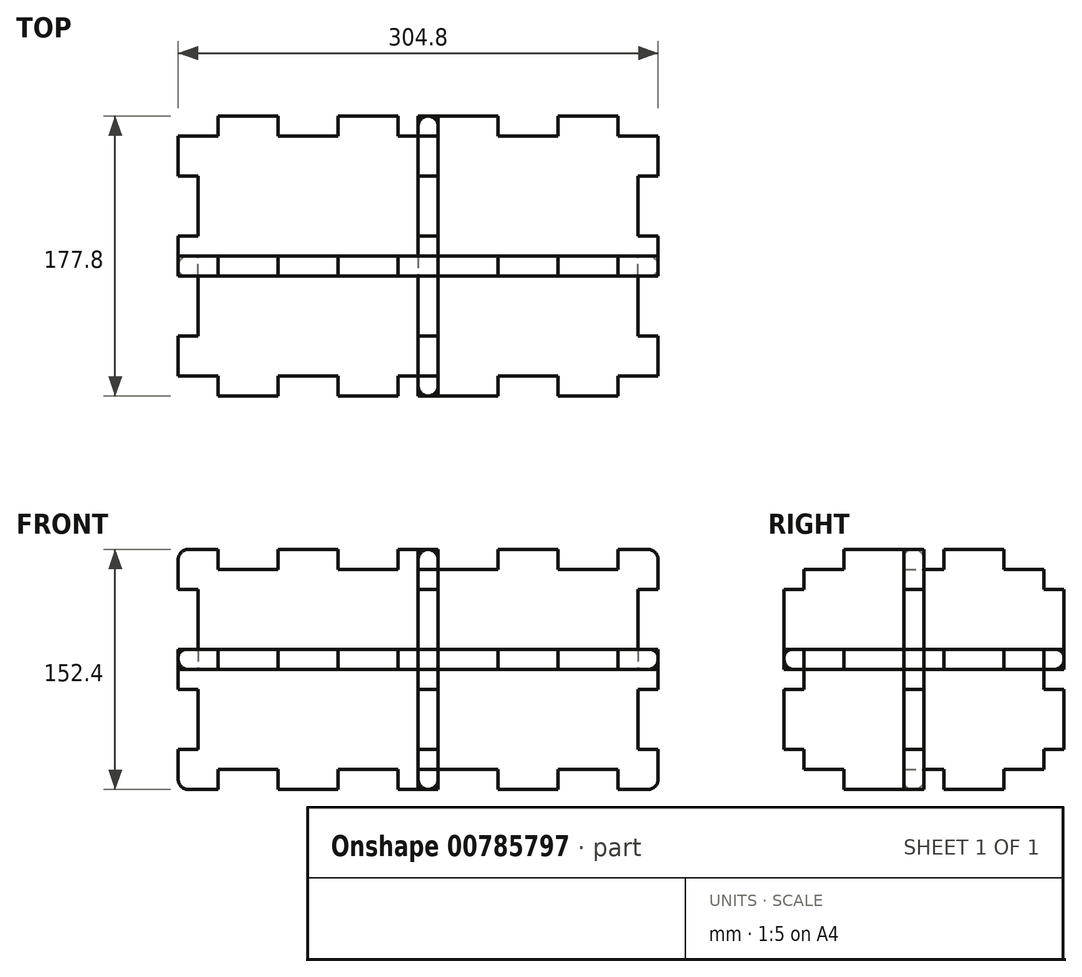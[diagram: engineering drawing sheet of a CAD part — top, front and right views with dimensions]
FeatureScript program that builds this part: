
annotation { "Feature Type Name" : "Feature", "Feature Type Description" : "" }
export const myFeature = defineFeature(function(context is Context, id is Id, definition is map)
    precondition{}
    {
        {
            var Q0;
            Q0=qCreatedBy(makeId("Top.planeOp"),FACE);
            var sketch = newSketch(context, id + "F0", { "sketchPlane" : qUnion([Q0])});
            skLineSegment(sketch, "E0.top", {"start": v(127, -88.9) * mm, "end": v(88.9, -88.9) * mm});
            skLineSegment(sketch, "E0.left", {"start": v(152.4, 76.2) * mm, "end": v(152.4, 50.8) * mm});
            skPoint(sketch, "E0.middle", {"position": v(0, 0) * mm});
            skLineSegment(sketch, "E1.0", {"start": v(152.4, 76.2) * mm, "end": v(127, 76.2) * mm});
            skLineSegment(sketch, "E1.1", {"start": v(139.7, 50.8) * mm, "end": v(139.7, 12.7) * mm});
            skLineSegment(sketch, "E1.3", {"start": v(-139.7, 50.8) * mm, "end": v(-139.7, 12.7) * mm});
            skLineSegment(sketch, "E2", {"start": v(-12.7, 76.2) * mm, "end": v(-12.7, 88.9) * mm});
            skLineSegment(sketch, "E3", {"start": v(-50.8, 76.2) * mm, "end": v(-50.8, 88.9) * mm});
            skLineSegment(sketch, "E4", {"start": v(-88.9, 76.2) * mm, "end": v(-88.9, 88.9) * mm});
            skLineSegment(sketch, "E5", {"start": v(-127, 88.9) * mm, "end": v(-127, 76.2) * mm});
            skLineSegment(sketch, "E6.MirrorCS", {"start": v(12.7, 76.2) * mm, "end": v(12.7, 88.9) * mm});
            skLineSegment(sketch, "E7.MirrorCS", {"start": v(50.8, 76.2) * mm, "end": v(50.8, 88.9) * mm});
            skLineSegment(sketch, "E8.MirrorCS", {"start": v(88.9, 76.2) * mm, "end": v(88.9, 88.9) * mm});
            skLineSegment(sketch, "E9.MirrorCS", {"start": v(127, 88.9) * mm, "end": v(127, 76.2) * mm});
            skLineSegment(sketch, "E10.trimOffspring", {"start": v(-12.7, 88.9) * mm, "end": v(-50.8, 88.9) * mm});
            skLineSegment(sketch, "E11.trimOffspring", {"start": v(-50.8, 76.2) * mm, "end": v(-88.9, 76.2) * mm});
            skLineSegment(sketch, "E12.trimOffspring", {"start": v(88.9, 76.2) * mm, "end": v(50.8, 76.2) * mm});
            skLineSegment(sketch, "E13.trimOffspring", {"start": v(127, 88.9) * mm, "end": v(88.9, 88.9) * mm});
            skLineSegment(sketch, "E14", {"start": v(-139.7, 12.7) * mm, "end": v(-152.4, 12.7) * mm});
            skLineSegment(sketch, "E15", {"start": v(-139.7, 50.8) * mm, "end": v(-152.4, 50.8) * mm});
            skLineSegment(sketch, "E16", {"start": v(-127, 76.2) * mm, "end": v(-152.4, 76.2) * mm});
            skLineSegment(sketch, "E17.trimOffspring", {"start": v(-88.9, 88.9) * mm, "end": v(-127, 88.9) * mm});
            skLineSegment(sketch, "E18.trimOffspring", {"start": v(12.7, 76.2) * mm, "end": v(-12.7, 76.2) * mm});
            skLineSegment(sketch, "E19.trimOffspring", {"start": v(50.8, 88.9) * mm, "end": v(12.7, 88.9) * mm});
            skPoint(sketch, "E20.orphan", {"position": v(152.4, 88.9) * mm});
            skLineSegment(sketch, "E21.MirrorCS", {"start": v(-139.7, -12.7) * mm, "end": v(-152.4, -12.7) * mm});
            skLineSegment(sketch, "E22.MirrorCS", {"start": v(-139.7, -50.8) * mm, "end": v(-152.4, -50.8) * mm});
            skLineSegment(sketch, "E23.MirrorCS", {"start": v(-127, -76.2) * mm, "end": v(-152.4, -76.2) * mm});
            skPoint(sketch, "E24.orphan", {"position": v(-127, -76.2) * mm});
            skLineSegment(sketch, "E25.trimOffspring", {"start": v(-139.7, -12.7) * mm, "end": v(-139.7, -50.8) * mm});
            skLineSegment(sketch, "E26.trimOffspring", {"start": v(-152.4, 12.7) * mm, "end": v(-152.4, -12.7) * mm});
            skLineSegment(sketch, "E27.trimOffspring", {"start": v(-152.4, -50.8) * mm, "end": v(-152.4, -76.2) * mm});
            skLineSegment(sketch, "E28.MirrorCS", {"start": v(-127, -88.9) * mm, "end": v(-127, -76.2) * mm});
            skLineSegment(sketch, "E29.MirrorCS", {"start": v(-88.9, -76.2) * mm, "end": v(-88.9, -88.9) * mm});
            skLineSegment(sketch, "E30.MirrorCS", {"start": v(-50.8, -76.2) * mm, "end": v(-88.9, -76.2) * mm});
            skLineSegment(sketch, "E31.MirrorCS", {"start": v(-50.8, -76.2) * mm, "end": v(-50.8, -88.9) * mm});
            skLineSegment(sketch, "E32.MirrorCS", {"start": v(-12.7, -76.2) * mm, "end": v(-12.7, -88.9) * mm});
            skLineSegment(sketch, "E33.MirrorCS", {"start": v(12.7, -76.2) * mm, "end": v(-12.7, -76.2) * mm});
            skLineSegment(sketch, "E34.MirrorCS", {"start": v(12.7, -76.2) * mm, "end": v(12.7, -88.9) * mm});
            skLineSegment(sketch, "E35.MirrorCS", {"start": v(50.8, -76.2) * mm, "end": v(50.8, -88.9) * mm});
            skLineSegment(sketch, "E36.MirrorCS", {"start": v(88.9, -76.2) * mm, "end": v(50.8, -76.2) * mm});
            skLineSegment(sketch, "E37.MirrorCS", {"start": v(88.9, -76.2) * mm, "end": v(88.9, -88.9) * mm});
            skLineSegment(sketch, "E38.MirrorCS", {"start": v(127, -88.9) * mm, "end": v(127, -76.2) * mm});
            skLineSegment(sketch, "E39.MirrorCS", {"start": v(152.4, -76.2) * mm, "end": v(127, -76.2) * mm});
            skLineSegment(sketch, "E40.trimOffspring", {"start": v(-88.9, -88.9) * mm, "end": v(-127, -88.9) * mm});
            skLineSegment(sketch, "E41.trimOffspring", {"start": v(-12.7, -88.9) * mm, "end": v(-50.8, -88.9) * mm});
            skLineSegment(sketch, "E42.trimOffspring", {"start": v(50.8, -88.9) * mm, "end": v(12.7, -88.9) * mm});
            skPoint(sketch, "E43.orphan", {"position": v(-152.4, -88.9) * mm});
            skLineSegment(sketch, "E44", {"start": v(-152.4, 76.2) * mm, "end": v(-152.4, 50.8) * mm});
            skLineSegment(sketch, "E45.MirrorCS", {"start": v(139.7, 50.8) * mm, "end": v(152.4, 50.8) * mm});
            skLineSegment(sketch, "E46.MirrorCS", {"start": v(139.7, 12.7) * mm, "end": v(152.4, 12.7) * mm});
            skLineSegment(sketch, "E47.MirrorCS", {"start": v(139.7, -12.7) * mm, "end": v(152.4, -12.7) * mm});
            skLineSegment(sketch, "E48.MirrorCS", {"start": v(139.7, -12.7) * mm, "end": v(139.7, -50.8) * mm});
            skLineSegment(sketch, "E49.MirrorCS", {"start": v(139.7, -50.8) * mm, "end": v(152.4, -50.8) * mm});
            skLineSegment(sketch, "E50.trimOffspring", {"start": v(152.4, 12.7) * mm, "end": v(152.4, -12.7) * mm});
            skLineSegment(sketch, "E51.trimOffspring", {"start": v(152.4, -50.8) * mm, "end": v(152.4, -76.2) * mm});
            skSolve(sketch);
        }
        {
            var Q0;
            Q0=makeQuery(id+"F0.imprint","IMPRINT",FACE,{"disambiguationData":[TD([[makeQuery(id+"F0.imprint","IMPRINT",EDGE,{"derivedFrom":sQuery(id+"F0.wireOp",EDGE,"E0.top")}),-1.0]])]});
            extrude(context, id + "F1", {"entities" : qUnion([Q0]), "depth" : 12.7 * mm, "offsetDistance" : 25.4 * mm});
        }
        {
            var Q0;
            Q0=makeQuery(id+"F1.opExtrude","SWEPT_BODY",BODY,{"disambiguationData":[OSD([sQuery(id+"F0.wireOp",EDGE,"E0.top"),sQuery(id+"F0.wireOp",EDGE,"E0.left"),sQuery(id+"F0.wireOp",EDGE,"E1.0"),sQuery(id+"F0.wireOp",EDGE,"E1.3"),sQuery(id+"F0.wireOp",EDGE,"E2"),sQuery(id+"F0.wireOp",EDGE,"E3"),sQuery(id+"F0.wireOp",EDGE,"E4"),sQuery(id+"F0.wireOp",EDGE,"E5"),sQuery(id+"F0.wireOp",EDGE,"E6.MirrorCS"),sQuery(id+"F0.wireOp",EDGE,"E7.MirrorCS"),sQuery(id+"F0.wireOp",EDGE,"E8.MirrorCS"),sQuery(id+"F0.wireOp",EDGE,"E9.MirrorCS"),sQuery(id+"F0.wireOp",EDGE,"E10.trimOffspring"),sQuery(id+"F0.wireOp",EDGE,"E11.trimOffspring"),sQuery(id+"F0.wireOp",EDGE,"E12.trimOffspring"),sQuery(id+"F0.wireOp",EDGE,"E13.trimOffspring"),sQuery(id+"F0.wireOp",EDGE,"E14"),sQuery(id+"F0.wireOp",EDGE,"E15"),sQuery(id+"F0.wireOp",EDGE,"E16"),sQuery(id+"F0.wireOp",EDGE,"E17.trimOffspring"),sQuery(id+"F0.wireOp",EDGE,"E18.trimOffspring"),sQuery(id+"F0.wireOp",EDGE,"E19.trimOffspring"),sQuery(id+"F0.wireOp",EDGE,"E21.MirrorCS"),sQuery(id+"F0.wireOp",EDGE,"E22.MirrorCS"),sQuery(id+"F0.wireOp",EDGE,"E23.MirrorCS"),sQuery(id+"F0.wireOp",EDGE,"E25.trimOffspring"),sQuery(id+"F0.wireOp",EDGE,"E26.trimOffspring"),sQuery(id+"F0.wireOp",EDGE,"E27.trimOffspring"),sQuery(id+"F0.wireOp",EDGE,"E28.MirrorCS"),sQuery(id+"F0.wireOp",EDGE,"E29.MirrorCS"),sQuery(id+"F0.wireOp",EDGE,"E30.MirrorCS"),sQuery(id+"F0.wireOp",EDGE,"E31.MirrorCS"),sQuery(id+"F0.wireOp",EDGE,"E32.MirrorCS"),sQuery(id+"F0.wireOp",EDGE,"E33.MirrorCS"),sQuery(id+"F0.wireOp",EDGE,"E34.MirrorCS"),sQuery(id+"F0.wireOp",EDGE,"E35.MirrorCS"),sQuery(id+"F0.wireOp",EDGE,"E36.MirrorCS"),sQuery(id+"F0.wireOp",EDGE,"E37.MirrorCS"),sQuery(id+"F0.wireOp",EDGE,"E38.MirrorCS"),sQuery(id+"F0.wireOp",EDGE,"E39.MirrorCS"),sQuery(id+"F0.wireOp",EDGE,"E40.trimOffspring"),sQuery(id+"F0.wireOp",EDGE,"E41.trimOffspring"),sQuery(id+"F0.wireOp",EDGE,"E42.trimOffspring"),sQuery(id+"F0.wireOp",EDGE,"E44"),sQuery(id+"F0.wireOp",EDGE,"E1.1"),sQuery(id+"F0.wireOp",EDGE,"E45.MirrorCS"),sQuery(id+"F0.wireOp",EDGE,"E46.MirrorCS"),sQuery(id+"F0.wireOp",EDGE,"E47.MirrorCS"),sQuery(id+"F0.wireOp",EDGE,"E49.MirrorCS"),sQuery(id+"F0.wireOp",EDGE,"E50.trimOffspring"),sQuery(id+"F0.wireOp",EDGE,"E48.MirrorCS"),sQuery(id+"F0.wireOp",EDGE,"E51.trimOffspring")])]});
            transform(context, id + "F2", {"entities" : qUnion([Q0]), "transformType" : TransformType.TRANSLATION_3D, "dx" : 0 * mm, "dy" : 0 * mm, "dz" : 0 * mm, "makeCopy" : true});
        }
        {
            var Q0;
            Q0=qCreatedBy(makeId("Front.planeOp"),FACE);
            var sketch = newSketch(context, id + "F3", { "sketchPlane" : qUnion([Q0])});
            skLineSegment(sketch, "E52.bottom", {"start": v(152.4, 76.2) * mm, "end": v(127, 76.2) * mm});
            skLineSegment(sketch, "E52.top", {"start": v(152.4, -76.2) * mm, "end": v(127, -76.2) * mm});
            skLineSegment(sketch, "E52.left", {"start": v(152.4, 76.2) * mm, "end": v(152.4, 50.8) * mm});
            skLineSegment(sketch, "E52.right", {"start": v(-152.4, 76.2) * mm, "end": v(-152.4, 50.8) * mm});
            skPoint(sketch, "E52.middle", {"position": v(0, 0) * mm});
            skLineSegment(sketch, "E53.0", {"start": v(127, 63.5) * mm, "end": v(88.9, 63.5) * mm});
            skLineSegment(sketch, "E53.1", {"start": v(139.7, 50.8) * mm, "end": v(139.7, 12.7) * mm});
            skLineSegment(sketch, "E53.2", {"start": v(127, -63.5) * mm, "end": v(88.9, -63.5) * mm});
            skLineSegment(sketch, "E53.3", {"start": v(-139.7, 50.8) * mm, "end": v(-139.7, 12.7) * mm});
            skLineSegment(sketch, "E54", {"start": v(-12.7, 63.5) * mm, "end": v(-12.7, 76.2) * mm});
            skLineSegment(sketch, "E55.0", {"start": v(-50.8, 63.5) * mm, "end": v(-50.8, 76.2) * mm});
            skLineSegment(sketch, "E56.0", {"start": v(-88.9, 63.5) * mm, "end": v(-88.9, 76.2) * mm});
            skLineSegment(sketch, "E57.0", {"start": v(-127, 63.5) * mm, "end": v(-127, 76.2) * mm});
            skLineSegment(sketch, "E58.0", {"start": v(12.7, 63.5) * mm, "end": v(12.7, 76.2) * mm});
            skLineSegment(sketch, "E59.0", {"start": v(50.8, 63.5) * mm, "end": v(50.8, 76.2) * mm});
            skLineSegment(sketch, "E60.0", {"start": v(88.9, 63.5) * mm, "end": v(88.9, 76.2) * mm});
            skLineSegment(sketch, "E61.0", {"start": v(127, 63.5) * mm, "end": v(127, 76.2) * mm});
            skLineSegment(sketch, "E62.MirrorCS", {"start": v(-127, -63.5) * mm, "end": v(-127, -76.2) * mm});
            skLineSegment(sketch, "E63.MirrorCS", {"start": v(-88.9, -63.5) * mm, "end": v(-88.9, -76.2) * mm});
            skLineSegment(sketch, "E64.MirrorCS", {"start": v(-50.8, -63.5) * mm, "end": v(-50.8, -76.2) * mm});
            skLineSegment(sketch, "E65.MirrorCS", {"start": v(-12.7, -63.5) * mm, "end": v(-12.7, -76.2) * mm});
            skLineSegment(sketch, "E66.MirrorCS", {"start": v(12.7, -63.5) * mm, "end": v(12.7, -76.2) * mm});
            skLineSegment(sketch, "E67.MirrorCS", {"start": v(50.8, -63.5) * mm, "end": v(50.8, -76.2) * mm});
            skLineSegment(sketch, "E68.MirrorCS", {"start": v(88.9, -63.5) * mm, "end": v(88.9, -76.2) * mm});
            skLineSegment(sketch, "E69.MirrorCS", {"start": v(127, -63.5) * mm, "end": v(127, -76.2) * mm});
            skLineSegment(sketch, "E70", {"start": v(-152.4, 12.7) * mm, "end": v(-139.7, 12.7) * mm});
            skLineSegment(sketch, "E71.0", {"start": v(-152.4, 50.8) * mm, "end": v(-139.7, 50.8) * mm});
            skLineSegment(sketch, "E72.MirrorCS", {"start": v(-152.4, -50.8) * mm, "end": v(-139.7, -50.8) * mm});
            skLineSegment(sketch, "E73.MirrorCS", {"start": v(-152.4, -12.7) * mm, "end": v(-139.7, -12.7) * mm});
            skLineSegment(sketch, "E74.MirrorCS", {"start": v(152.4, -12.7) * mm, "end": v(139.7, -12.7) * mm});
            skLineSegment(sketch, "E75.MirrorCS", {"start": v(152.4, 12.7) * mm, "end": v(139.7, 12.7) * mm});
            skLineSegment(sketch, "E76.MirrorCS", {"start": v(152.4, 50.8) * mm, "end": v(139.7, 50.8) * mm});
            skLineSegment(sketch, "E77.MirrorCS", {"start": v(152.4, -50.8) * mm, "end": v(139.7, -50.8) * mm});
            skLineSegment(sketch, "E78.trimOffspring", {"start": v(-127, 76.2) * mm, "end": v(-152.4, 76.2) * mm});
            skLineSegment(sketch, "E79.trimOffspring", {"start": v(-152.4, 12.7) * mm, "end": v(-152.4, -12.7) * mm});
            skLineSegment(sketch, "E80.trimOffspring", {"start": v(-88.9, 63.5) * mm, "end": v(-127, 63.5) * mm});
            skLineSegment(sketch, "E81.trimOffspring", {"start": v(-50.8, 76.2) * mm, "end": v(-88.9, 76.2) * mm});
            skLineSegment(sketch, "E82.trimOffspring", {"start": v(-12.7, 63.5) * mm, "end": v(-50.8, 63.5) * mm});
            skLineSegment(sketch, "E83.trimOffspring", {"start": v(12.7, 76.2) * mm, "end": v(-12.7, 76.2) * mm});
            skLineSegment(sketch, "E84.trimOffspring", {"start": v(50.8, 63.5) * mm, "end": v(12.7, 63.5) * mm});
            skLineSegment(sketch, "E85.trimOffspring", {"start": v(88.9, 76.2) * mm, "end": v(50.8, 76.2) * mm});
            skLineSegment(sketch, "E86.trimOffspring", {"start": v(-139.7, -12.7) * mm, "end": v(-139.7, -50.8) * mm});
            skLineSegment(sketch, "E87.trimOffspring", {"start": v(-152.4, -50.8) * mm, "end": v(-152.4, -76.2) * mm});
            skLineSegment(sketch, "E88.trimOffspring", {"start": v(-127, -76.2) * mm, "end": v(-152.4, -76.2) * mm});
            skLineSegment(sketch, "E89.trimOffspring", {"start": v(-88.9, -63.5) * mm, "end": v(-127, -63.5) * mm});
            skLineSegment(sketch, "E90.trimOffspring", {"start": v(-50.8, -76.2) * mm, "end": v(-88.9, -76.2) * mm});
            skLineSegment(sketch, "E91.trimOffspring", {"start": v(-12.7, -63.5) * mm, "end": v(-50.8, -63.5) * mm});
            skLineSegment(sketch, "E92.trimOffspring", {"start": v(12.7, -76.2) * mm, "end": v(-12.7, -76.2) * mm});
            skLineSegment(sketch, "E93.trimOffspring", {"start": v(50.8, -63.5) * mm, "end": v(12.7, -63.5) * mm});
            skLineSegment(sketch, "E94.trimOffspring", {"start": v(88.9, -76.2) * mm, "end": v(50.8, -76.2) * mm});
            skLineSegment(sketch, "E95.trimOffspring", {"start": v(152.4, 12.7) * mm, "end": v(152.4, -12.7) * mm});
            skLineSegment(sketch, "E96.trimOffspring", {"start": v(139.7, -12.7) * mm, "end": v(139.7, -50.8) * mm});
            skLineSegment(sketch, "E97.trimOffspring", {"start": v(152.4, -50.8) * mm, "end": v(152.4, -76.2) * mm});
            skSolve(sketch);
        }
        {
            var Q0;
            Q0=makeQuery(id+"F3.imprint","IMPRINT",FACE,{"disambiguationData":[TD([[makeQuery(id+"F3.imprint","IMPRINT",EDGE,{"derivedFrom":sQuery(id+"F3.wireOp",EDGE,"E52.bottom")}),1.0]])]});
            extrude(context, id + "F4", {"entities" : qUnion([Q0]), "depth" : 12.7 * mm, "offsetDistance" : 25.4 * mm});
        }
        {
            var Q0;
            Q0=makeQuery(id+"F4.opExtrude","SWEPT_BODY",BODY,{"disambiguationData":[OSD([sQuery(id+"F3.wireOp",EDGE,"E52.bottom"),sQuery(id+"F3.wireOp",EDGE,"E52.top"),sQuery(id+"F3.wireOp",EDGE,"E52.left"),sQuery(id+"F3.wireOp",EDGE,"E52.right"),sQuery(id+"F3.wireOp",EDGE,"E53.0"),sQuery(id+"F3.wireOp",EDGE,"E53.1"),sQuery(id+"F3.wireOp",EDGE,"E53.2"),sQuery(id+"F3.wireOp",EDGE,"E53.3"),sQuery(id+"F3.wireOp",EDGE,"E54"),sQuery(id+"F3.wireOp",EDGE,"E55.0"),sQuery(id+"F3.wireOp",EDGE,"E56.0"),sQuery(id+"F3.wireOp",EDGE,"E57.0"),sQuery(id+"F3.wireOp",EDGE,"E58.0"),sQuery(id+"F3.wireOp",EDGE,"E59.0"),sQuery(id+"F3.wireOp",EDGE,"E60.0"),sQuery(id+"F3.wireOp",EDGE,"E61.0"),sQuery(id+"F3.wireOp",EDGE,"E62.MirrorCS"),sQuery(id+"F3.wireOp",EDGE,"E63.MirrorCS"),sQuery(id+"F3.wireOp",EDGE,"E64.MirrorCS"),sQuery(id+"F3.wireOp",EDGE,"E65.MirrorCS"),sQuery(id+"F3.wireOp",EDGE,"E66.MirrorCS"),sQuery(id+"F3.wireOp",EDGE,"E67.MirrorCS"),sQuery(id+"F3.wireOp",EDGE,"E68.MirrorCS"),sQuery(id+"F3.wireOp",EDGE,"E69.MirrorCS"),sQuery(id+"F3.wireOp",EDGE,"E70"),sQuery(id+"F3.wireOp",EDGE,"E71.0"),sQuery(id+"F3.wireOp",EDGE,"E72.MirrorCS"),sQuery(id+"F3.wireOp",EDGE,"E73.MirrorCS"),sQuery(id+"F3.wireOp",EDGE,"E74.MirrorCS"),sQuery(id+"F3.wireOp",EDGE,"E75.MirrorCS"),sQuery(id+"F3.wireOp",EDGE,"E76.MirrorCS"),sQuery(id+"F3.wireOp",EDGE,"E77.MirrorCS"),sQuery(id+"F3.wireOp",EDGE,"E78.trimOffspring"),sQuery(id+"F3.wireOp",EDGE,"E79.trimOffspring"),sQuery(id+"F3.wireOp",EDGE,"E80.trimOffspring"),sQuery(id+"F3.wireOp",EDGE,"E81.trimOffspring"),sQuery(id+"F3.wireOp",EDGE,"E82.trimOffspring"),sQuery(id+"F3.wireOp",EDGE,"E83.trimOffspring"),sQuery(id+"F3.wireOp",EDGE,"E84.trimOffspring"),sQuery(id+"F3.wireOp",EDGE,"E85.trimOffspring"),sQuery(id+"F3.wireOp",EDGE,"E86.trimOffspring"),sQuery(id+"F3.wireOp",EDGE,"E87.trimOffspring"),sQuery(id+"F3.wireOp",EDGE,"E88.trimOffspring"),sQuery(id+"F3.wireOp",EDGE,"E89.trimOffspring"),sQuery(id+"F3.wireOp",EDGE,"E90.trimOffspring"),sQuery(id+"F3.wireOp",EDGE,"E91.trimOffspring"),sQuery(id+"F3.wireOp",EDGE,"E92.trimOffspring"),sQuery(id+"F3.wireOp",EDGE,"E93.trimOffspring"),sQuery(id+"F3.wireOp",EDGE,"E94.trimOffspring"),sQuery(id+"F3.wireOp",EDGE,"E95.trimOffspring"),sQuery(id+"F3.wireOp",EDGE,"E96.trimOffspring"),sQuery(id+"F3.wireOp",EDGE,"E97.trimOffspring")])]});
            transform(context, id + "F5", {"entities" : qUnion([Q0]), "transformType" : TransformType.TRANSLATION_3D, "dx" : 0 * mm, "dy" : 0 * mm, "dz" : 0 * mm, "makeCopy" : true});
        }
        {
            var Q0;
            Q0=qCreatedBy(makeId("Right.planeOp"),FACE);
            var sketch = newSketch(context, id + "F6", { "sketchPlane" : qUnion([Q0])});
            skLineSegment(sketch, "E98.bottom", {"start": v(50.8, 76.2) * mm, "end": v(12.7, 76.2) * mm});
            skLineSegment(sketch, "E98.top", {"start": v(50.8, -76.2) * mm, "end": v(12.7, -76.2) * mm});
            skLineSegment(sketch, "E98.left", {"start": v(88.9, 50.8) * mm, "end": v(88.9, 12.7) * mm});
            skLineSegment(sketch, "E98.right", {"start": v(-88.9, 50.8) * mm, "end": v(-88.9, 12.7) * mm});
            skPoint(sketch, "E98.middle", {"position": v(0, 0) * mm});
            skLineSegment(sketch, "E99.0", {"start": v(76.2, 63.5) * mm, "end": v(50.8, 63.5) * mm});
            skLineSegment(sketch, "E99.1", {"start": v(76.2, 63.5) * mm, "end": v(76.2, 50.8) * mm});
            skLineSegment(sketch, "E99.2", {"start": v(76.2, -63.5) * mm, "end": v(50.8, -63.5) * mm});
            skLineSegment(sketch, "E99.3", {"start": v(-76.2, 63.5) * mm, "end": v(-76.2, 50.8) * mm});
            skLineSegment(sketch, "E100", {"start": v(-88.9, 12.7) * mm, "end": v(-76.2, 12.7) * mm});
            skLineSegment(sketch, "E101", {"start": v(-88.9, 50.8) * mm, "end": v(-76.2, 50.8) * mm});
            skLineSegment(sketch, "E102", {"start": v(-12.7, 63.5) * mm, "end": v(-12.7, 76.2) * mm});
            skLineSegment(sketch, "E103", {"start": v(-50.8, 63.5) * mm, "end": v(-50.8, 76.2) * mm});
            skLineSegment(sketch, "E104.MirrorCS", {"start": v(12.7, 63.5) * mm, "end": v(12.7, 76.2) * mm});
            skLineSegment(sketch, "E105.MirrorCS", {"start": v(50.8, 63.5) * mm, "end": v(50.8, 76.2) * mm});
            skLineSegment(sketch, "E106.MirrorCS", {"start": v(88.9, 50.8) * mm, "end": v(76.2, 50.8) * mm});
            skLineSegment(sketch, "E107.MirrorCS", {"start": v(88.9, 12.7) * mm, "end": v(76.2, 12.7) * mm});
            skLineSegment(sketch, "E108.MirrorCS", {"start": v(-88.9, -12.7) * mm, "end": v(-76.2, -12.7) * mm});
            skLineSegment(sketch, "E109.MirrorCS", {"start": v(-88.9, -50.8) * mm, "end": v(-76.2, -50.8) * mm});
            skLineSegment(sketch, "E110.MirrorCS", {"start": v(-50.8, -63.5) * mm, "end": v(-50.8, -76.2) * mm});
            skLineSegment(sketch, "E111.MirrorCS", {"start": v(-12.7, -63.5) * mm, "end": v(-12.7, -76.2) * mm});
            skLineSegment(sketch, "E112.MirrorCS", {"start": v(12.7, -63.5) * mm, "end": v(12.7, -76.2) * mm});
            skLineSegment(sketch, "E113.MirrorCS", {"start": v(50.8, -63.5) * mm, "end": v(50.8, -76.2) * mm});
            skLineSegment(sketch, "E114.MirrorCS", {"start": v(88.9, -50.8) * mm, "end": v(76.2, -50.8) * mm});
            skLineSegment(sketch, "E115.MirrorCS", {"start": v(88.9, -12.7) * mm, "end": v(76.2, -12.7) * mm});
            skLineSegment(sketch, "E116.trimOffspring", {"start": v(-88.9, -12.7) * mm, "end": v(-88.9, -50.8) * mm});
            skLineSegment(sketch, "E117.trimOffspring", {"start": v(-76.2, 12.7) * mm, "end": v(-76.2, -12.7) * mm});
            skLineSegment(sketch, "E118.trimOffspring", {"start": v(-76.2, -50.8) * mm, "end": v(-76.2, -63.5) * mm});
            skLineSegment(sketch, "E119.trimOffspring", {"start": v(76.2, -50.8) * mm, "end": v(76.2, -63.5) * mm});
            skLineSegment(sketch, "E120.trimOffspring", {"start": v(88.9, -12.7) * mm, "end": v(88.9, -50.8) * mm});
            skLineSegment(sketch, "E121.trimOffspring", {"start": v(76.2, 12.7) * mm, "end": v(76.2, -12.7) * mm});
            skLineSegment(sketch, "E122.trimOffspring", {"start": v(-12.7, 76.2) * mm, "end": v(-50.8, 76.2) * mm});
            skLineSegment(sketch, "E123.trimOffspring", {"start": v(-50.8, 63.5) * mm, "end": v(-76.2, 63.5) * mm});
            skLineSegment(sketch, "E124.trimOffspring", {"start": v(12.7, 63.5) * mm, "end": v(-12.7, 63.5) * mm});
            skLineSegment(sketch, "E125.trimOffspring", {"start": v(-12.7, -76.2) * mm, "end": v(-50.8, -76.2) * mm});
            skLineSegment(sketch, "E126.trimOffspring", {"start": v(-50.8, -63.5) * mm, "end": v(-76.2, -63.5) * mm});
            skLineSegment(sketch, "E127.trimOffspring", {"start": v(12.7, -63.5) * mm, "end": v(-12.7, -63.5) * mm});
            skPoint(sketch, "E128.orphan", {"position": v(-88.9, -76.2) * mm});
            skPoint(sketch, "E129.orphan", {"position": v(88.9, -76.2) * mm});
            skPoint(sketch, "E130.orphan", {"position": v(-88.9, 76.2) * mm});
            skPoint(sketch, "E131.orphan", {"position": v(88.9, 76.2) * mm});
            skSolve(sketch);
        }
        {
            var Q0;
            Q0=makeQuery(id+"F6.imprint","IMPRINT",FACE,{"disambiguationData":[TD([[makeQuery(id+"F6.imprint","IMPRINT",EDGE,{"derivedFrom":sQuery(id+"F6.wireOp",EDGE,"E98.bottom")}),1.0]])]});
            extrude(context, id + "F7", {"entities" : qUnion([Q0]), "depth" : 12.7 * mm, "offsetDistance" : 25.4 * mm});
        }
        {
            var Q0;
            Q0=makeQuery(id+"F7.opExtrude","SWEPT_BODY",BODY,{"disambiguationData":[OSD([sQuery(id+"F6.wireOp",EDGE,"E98.bottom"),sQuery(id+"F6.wireOp",EDGE,"E98.top"),sQuery(id+"F6.wireOp",EDGE,"E98.left"),sQuery(id+"F6.wireOp",EDGE,"E98.right"),sQuery(id+"F6.wireOp",EDGE,"E99.0"),sQuery(id+"F6.wireOp",EDGE,"E99.1"),sQuery(id+"F6.wireOp",EDGE,"E99.2"),sQuery(id+"F6.wireOp",EDGE,"E99.3"),sQuery(id+"F6.wireOp",EDGE,"E100"),sQuery(id+"F6.wireOp",EDGE,"E101"),sQuery(id+"F6.wireOp",EDGE,"E102"),sQuery(id+"F6.wireOp",EDGE,"E103"),sQuery(id+"F6.wireOp",EDGE,"E104.MirrorCS"),sQuery(id+"F6.wireOp",EDGE,"E105.MirrorCS"),sQuery(id+"F6.wireOp",EDGE,"E106.MirrorCS"),sQuery(id+"F6.wireOp",EDGE,"E107.MirrorCS"),sQuery(id+"F6.wireOp",EDGE,"E108.MirrorCS"),sQuery(id+"F6.wireOp",EDGE,"E109.MirrorCS"),sQuery(id+"F6.wireOp",EDGE,"E110.MirrorCS"),sQuery(id+"F6.wireOp",EDGE,"E111.MirrorCS"),sQuery(id+"F6.wireOp",EDGE,"E112.MirrorCS"),sQuery(id+"F6.wireOp",EDGE,"E113.MirrorCS"),sQuery(id+"F6.wireOp",EDGE,"E114.MirrorCS"),sQuery(id+"F6.wireOp",EDGE,"E115.MirrorCS"),sQuery(id+"F6.wireOp",EDGE,"E116.trimOffspring"),sQuery(id+"F6.wireOp",EDGE,"E117.trimOffspring"),sQuery(id+"F6.wireOp",EDGE,"E118.trimOffspring"),sQuery(id+"F6.wireOp",EDGE,"E119.trimOffspring"),sQuery(id+"F6.wireOp",EDGE,"E120.trimOffspring"),sQuery(id+"F6.wireOp",EDGE,"E121.trimOffspring"),sQuery(id+"F6.wireOp",EDGE,"E122.trimOffspring"),sQuery(id+"F6.wireOp",EDGE,"E123.trimOffspring"),sQuery(id+"F6.wireOp",EDGE,"E124.trimOffspring"),sQuery(id+"F6.wireOp",EDGE,"E125.trimOffspring"),sQuery(id+"F6.wireOp",EDGE,"E126.trimOffspring"),sQuery(id+"F6.wireOp",EDGE,"E127.trimOffspring")])]});
            transform(context, id + "F8", {"entities" : qUnion([Q0]), "transformType" : TransformType.TRANSLATION_3D, "dx" : 0 * mm, "dy" : 0 * mm, "dz" : 0 * mm, "makeCopy" : true});
        }
        {
            var Q0;
            Q0=makeQuery(id+"F8.opPattern","COPY",EDGE,{"derivedFrom":makeQuery(id+"F7.opExtrude","CAP_EDGE",EDGE,{"disambiguationData":[OSD([sQuery(id+"F6.wireOp",EDGE,"E122.trimOffspring")])],"isStart":false}),"instanceName":"1"});
            var Q1;
            Q1=makeQuery(id+"F8.opPattern","COPY",EDGE,{"derivedFrom":makeQuery(id+"F7.opExtrude","CAP_EDGE",EDGE,{"disambiguationData":[OSD([sQuery(id+"F6.wireOp",EDGE,"E98.bottom")])],"isStart":false}),"instanceName":"1"});
            var Q2;
            Q2=makeQuery(id+"F8.opPattern","COPY",EDGE,{"derivedFrom":makeQuery(id+"F7.opExtrude","CAP_EDGE",EDGE,{"disambiguationData":[OSD([sQuery(id+"F6.wireOp",EDGE,"E98.right")])],"isStart":false}),"instanceName":"1"});
            var Q3;
            Q3=makeQuery(id+"F8.opPattern","COPY",EDGE,{"derivedFrom":makeQuery(id+"F7.opExtrude","CAP_EDGE",EDGE,{"disambiguationData":[OSD([sQuery(id+"F6.wireOp",EDGE,"E116.trimOffspring")])],"isStart":false}),"instanceName":"1"});
            var Q4;
            Q4=makeQuery(id+"F8.opPattern","COPY",EDGE,{"derivedFrom":makeQuery(id+"F7.opExtrude","CAP_EDGE",EDGE,{"disambiguationData":[OSD([sQuery(id+"F6.wireOp",EDGE,"E98.left")])],"isStart":false}),"instanceName":"1"});
            var Q5;
            Q5=makeQuery(id+"F8.opPattern","COPY",EDGE,{"derivedFrom":makeQuery(id+"F7.opExtrude","CAP_EDGE",EDGE,{"disambiguationData":[OSD([sQuery(id+"F6.wireOp",EDGE,"E120.trimOffspring")])],"isStart":false}),"instanceName":"1"});
            var Q6;
            Q6=makeQuery(id+"F8.opPattern","COPY",EDGE,{"derivedFrom":makeQuery(id+"F7.opExtrude","CAP_EDGE",EDGE,{"disambiguationData":[OSD([sQuery(id+"F6.wireOp",EDGE,"E125.trimOffspring")])],"isStart":false}),"instanceName":"1"});
            var Q7;
            Q7=makeQuery(id+"F8.opPattern","COPY",EDGE,{"derivedFrom":makeQuery(id+"F7.opExtrude","CAP_EDGE",EDGE,{"disambiguationData":[OSD([sQuery(id+"F6.wireOp",EDGE,"E98.top")])],"isStart":false}),"instanceName":"1"});
            fillet(context, id + "F9", {"entities" : qUnion([Q0, Q1, Q2, Q3, Q4, Q5, Q6, Q7]), "radius" : 6.35 * mm, "tangentPropagation" : true, "allowEdgeOverflow" : false});
        }
        {
            var Q0;
            Q0=makeQuery(id+"F7.opExtrude","CAP_EDGE",EDGE,{"disambiguationData":[OSD([sQuery(id+"F6.wireOp",EDGE,"E98.left")])],"isStart":true});
            var Q1;
            Q1=makeQuery(id+"F7.opExtrude","CAP_EDGE",EDGE,{"disambiguationData":[OSD([sQuery(id+"F6.wireOp",EDGE,"E120.trimOffspring")])],"isStart":true});
            var Q2;
            Q2=makeQuery(id+"F7.opExtrude","CAP_EDGE",EDGE,{"disambiguationData":[OSD([sQuery(id+"F6.wireOp",EDGE,"E98.bottom")])],"isStart":true});
            var Q3;
            Q3=makeQuery(id+"F7.opExtrude","CAP_EDGE",EDGE,{"disambiguationData":[OSD([sQuery(id+"F6.wireOp",EDGE,"E122.trimOffspring")])],"isStart":true});
            var Q4;
            Q4=makeQuery(id+"F7.opExtrude","CAP_EDGE",EDGE,{"disambiguationData":[OSD([sQuery(id+"F6.wireOp",EDGE,"E98.right")])],"isStart":true});
            var Q5;
            Q5=makeQuery(id+"F7.opExtrude","CAP_EDGE",EDGE,{"disambiguationData":[OSD([sQuery(id+"F6.wireOp",EDGE,"E116.trimOffspring")])],"isStart":true});
            var Q6;
            Q6=makeQuery(id+"F7.opExtrude","CAP_EDGE",EDGE,{"disambiguationData":[OSD([sQuery(id+"F6.wireOp",EDGE,"E98.top")])],"isStart":true});
            var Q7;
            Q7=makeQuery(id+"F7.opExtrude","CAP_EDGE",EDGE,{"disambiguationData":[OSD([sQuery(id+"F6.wireOp",EDGE,"E125.trimOffspring")])],"isStart":true});
            fillet(context, id + "F10", {"entities" : qUnion([Q0, Q1, Q2, Q3, Q4, Q5, Q6, Q7]), "radius" : 6.35 * mm, "tangentPropagation" : true, "allowEdgeOverflow" : false});
        }
        {
            var Q0;
            Q0=makeQuery(id+"F5.opPattern","COPY",EDGE,{"derivedFrom":makeQuery(id+"F4.opExtrude","CAP_EDGE",EDGE,{"disambiguationData":[OSD([sQuery(id+"F3.wireOp",EDGE,"E85.trimOffspring")])],"isStart":true}),"instanceName":"1"});
            var Q1;
            Q1=makeQuery(id+"F5.opPattern","COPY",EDGE,{"derivedFrom":makeQuery(id+"F4.opExtrude","CAP_EDGE",EDGE,{"disambiguationData":[OSD([sQuery(id+"F3.wireOp",EDGE,"E83.trimOffspring")])],"isStart":true}),"instanceName":"1"});
            var Q2;
            Q2=makeQuery(id+"F5.opPattern","COPY",EDGE,{"derivedFrom":makeQuery(id+"F4.opExtrude","CAP_EDGE",EDGE,{"disambiguationData":[OSD([sQuery(id+"F3.wireOp",EDGE,"E81.trimOffspring")])],"isStart":true}),"instanceName":"1"});
            var Q3;
            Q3=makeQuery(id+"F5.opPattern","COPY",EDGE,{"derivedFrom":makeQuery(id+"F4.opExtrude","CAP_EDGE",EDGE,{"disambiguationData":[OSD([sQuery(id+"F3.wireOp",EDGE,"E78.trimOffspring")])],"isStart":true}),"instanceName":"1"});
            var Q4;
            Q4=makeQuery(id+"F5.opPattern","COPY",EDGE,{"derivedFrom":makeQuery(id+"F4.opExtrude","CAP_EDGE",EDGE,{"disambiguationData":[OSD([sQuery(id+"F3.wireOp",EDGE,"E52.right")])],"isStart":true}),"instanceName":"1"});
            var Q5;
            Q5=makeQuery(id+"F5.opPattern","COPY",EDGE,{"derivedFrom":makeQuery(id+"F4.opExtrude","CAP_EDGE",EDGE,{"disambiguationData":[OSD([sQuery(id+"F3.wireOp",EDGE,"E79.trimOffspring")])],"isStart":true}),"instanceName":"1"});
            var Q6;
            Q6=makeQuery(id+"F5.opPattern","COPY",EDGE,{"derivedFrom":makeQuery(id+"F4.opExtrude","CAP_EDGE",EDGE,{"disambiguationData":[OSD([sQuery(id+"F3.wireOp",EDGE,"E88.trimOffspring")])],"isStart":true}),"instanceName":"1"});
            var Q7;
            Q7=makeQuery(id+"F5.opPattern","COPY",EDGE,{"derivedFrom":makeQuery(id+"F4.opExtrude","CAP_EDGE",EDGE,{"disambiguationData":[OSD([sQuery(id+"F3.wireOp",EDGE,"E87.trimOffspring")])],"isStart":true}),"instanceName":"1"});
            var Q8;
            Q8=makeQuery(id+"F5.opPattern","COPY",EDGE,{"derivedFrom":makeQuery(id+"F4.opExtrude","CAP_EDGE",EDGE,{"disambiguationData":[OSD([sQuery(id+"F3.wireOp",EDGE,"E90.trimOffspring")])],"isStart":true}),"instanceName":"1"});
            var Q9;
            Q9=makeQuery(id+"F5.opPattern","COPY",EDGE,{"derivedFrom":makeQuery(id+"F4.opExtrude","CAP_EDGE",EDGE,{"disambiguationData":[OSD([sQuery(id+"F3.wireOp",EDGE,"E92.trimOffspring")])],"isStart":true}),"instanceName":"1"});
            var Q10;
            Q10=makeQuery(id+"F5.opPattern","COPY",EDGE,{"derivedFrom":makeQuery(id+"F4.opExtrude","CAP_EDGE",EDGE,{"disambiguationData":[OSD([sQuery(id+"F3.wireOp",EDGE,"E94.trimOffspring")])],"isStart":true}),"instanceName":"1"});
            var Q11;
            Q11=makeQuery(id+"F5.opPattern","COPY",EDGE,{"derivedFrom":makeQuery(id+"F4.opExtrude","CAP_EDGE",EDGE,{"disambiguationData":[OSD([sQuery(id+"F3.wireOp",EDGE,"E52.top")])],"isStart":true}),"instanceName":"1"});
            var Q12;
            Q12=makeQuery(id+"F5.opPattern","COPY",EDGE,{"derivedFrom":makeQuery(id+"F4.opExtrude","CAP_EDGE",EDGE,{"disambiguationData":[OSD([sQuery(id+"F3.wireOp",EDGE,"E97.trimOffspring")])],"isStart":true}),"instanceName":"1"});
            var Q13;
            Q13=makeQuery(id+"F5.opPattern","COPY",EDGE,{"derivedFrom":makeQuery(id+"F4.opExtrude","CAP_EDGE",EDGE,{"disambiguationData":[OSD([sQuery(id+"F3.wireOp",EDGE,"E95.trimOffspring")])],"isStart":true}),"instanceName":"1"});
            var Q14;
            Q14=makeQuery(id+"F5.opPattern","COPY",EDGE,{"derivedFrom":makeQuery(id+"F4.opExtrude","CAP_EDGE",EDGE,{"disambiguationData":[OSD([sQuery(id+"F3.wireOp",EDGE,"E52.left")])],"isStart":true}),"instanceName":"1"});
            var Q15;
            Q15=makeQuery(id+"F5.opPattern","COPY",EDGE,{"derivedFrom":makeQuery(id+"F4.opExtrude","CAP_EDGE",EDGE,{"disambiguationData":[OSD([sQuery(id+"F3.wireOp",EDGE,"E52.bottom")])],"isStart":true}),"instanceName":"1"});
            fillet(context, id + "F11", {"entities" : qUnion([Q0, Q1, Q2, Q3, Q4, Q5, Q6, Q7, Q8, Q9, Q10, Q11, Q12, Q13, Q14, Q15]), "radius" : 6.35 * mm, "tangentPropagation" : true, "allowEdgeOverflow" : false});
        }
        {
            var Q0;
            Q0=makeQuery(id+"F1.opExtrude","CAP_EDGE",EDGE,{"disambiguationData":[OSD([sQuery(id+"F0.wireOp",EDGE,"E0.left")])],"isStart":false});
            var Q1;
            Q1=makeQuery(id+"F1.opExtrude","CAP_EDGE",EDGE,{"disambiguationData":[OSD([sQuery(id+"F0.wireOp",EDGE,"E50.trimOffspring")])],"isStart":false});
            var Q2;
            Q2=makeQuery(id+"F1.opExtrude","CAP_EDGE",EDGE,{"disambiguationData":[OSD([sQuery(id+"F0.wireOp",EDGE,"E51.trimOffspring")])],"isStart":false});
            var Q3;
            Q3=makeQuery(id+"F1.opExtrude","CAP_EDGE",EDGE,{"disambiguationData":[OSD([sQuery(id+"F0.wireOp",EDGE,"E13.trimOffspring")])],"isStart":false});
            var Q4;
            Q4=makeQuery(id+"F1.opExtrude","CAP_EDGE",EDGE,{"disambiguationData":[OSD([sQuery(id+"F0.wireOp",EDGE,"E19.trimOffspring")])],"isStart":false});
            var Q5;
            Q5=makeQuery(id+"F1.opExtrude","CAP_EDGE",EDGE,{"disambiguationData":[OSD([sQuery(id+"F0.wireOp",EDGE,"E10.trimOffspring")])],"isStart":false});
            var Q6;
            Q6=makeQuery(id+"F1.opExtrude","CAP_EDGE",EDGE,{"disambiguationData":[OSD([sQuery(id+"F0.wireOp",EDGE,"E0.top")])],"isStart":false});
            var Q7;
            Q7=makeQuery(id+"F1.opExtrude","CAP_EDGE",EDGE,{"disambiguationData":[OSD([sQuery(id+"F0.wireOp",EDGE,"E42.trimOffspring")])],"isStart":false});
            var Q8;
            Q8=makeQuery(id+"F1.opExtrude","CAP_EDGE",EDGE,{"disambiguationData":[OSD([sQuery(id+"F0.wireOp",EDGE,"E41.trimOffspring")])],"isStart":false});
            var Q9;
            Q9=makeQuery(id+"F1.opExtrude","CAP_EDGE",EDGE,{"disambiguationData":[OSD([sQuery(id+"F0.wireOp",EDGE,"E40.trimOffspring")])],"isStart":false});
            var Q10;
            Q10=makeQuery(id+"F1.opExtrude","CAP_EDGE",EDGE,{"disambiguationData":[OSD([sQuery(id+"F0.wireOp",EDGE,"E17.trimOffspring")])],"isStart":false});
            var Q11;
            Q11=makeQuery(id+"F1.opExtrude","CAP_EDGE",EDGE,{"disambiguationData":[OSD([sQuery(id+"F0.wireOp",EDGE,"E44")])],"isStart":false});
            var Q12;
            Q12=makeQuery(id+"F1.opExtrude","CAP_EDGE",EDGE,{"disambiguationData":[OSD([sQuery(id+"F0.wireOp",EDGE,"E26.trimOffspring")])],"isStart":false});
            var Q13;
            Q13=makeQuery(id+"F1.opExtrude","CAP_EDGE",EDGE,{"disambiguationData":[OSD([sQuery(id+"F0.wireOp",EDGE,"E27.trimOffspring")])],"isStart":false});
            fillet(context, id + "F12", {"entities" : qUnion([Q0, Q1, Q2, Q3, Q4, Q5, Q6, Q7, Q8, Q9, Q10, Q11, Q12, Q13]), "radius" : 5.08 * mm, "tangentPropagation" : true, "allowEdgeOverflow" : false});
        }
        {
            var Q0;
            Q0=makeQuery(id+"F2.opPattern","COPY",EDGE,{"derivedFrom":makeQuery(id+"F1.opExtrude","CAP_EDGE",EDGE,{"disambiguationData":[OSD([sQuery(id+"F0.wireOp",EDGE,"E44")])],"isStart":true}),"instanceName":"1"});
            var Q1;
            Q1=makeQuery(id+"F2.opPattern","COPY",EDGE,{"derivedFrom":makeQuery(id+"F1.opExtrude","CAP_EDGE",EDGE,{"disambiguationData":[OSD([sQuery(id+"F0.wireOp",EDGE,"E17.trimOffspring")])],"isStart":true}),"instanceName":"1"});
            var Q2;
            Q2=makeQuery(id+"F2.opPattern","COPY",EDGE,{"derivedFrom":makeQuery(id+"F1.opExtrude","CAP_EDGE",EDGE,{"disambiguationData":[OSD([sQuery(id+"F0.wireOp",EDGE,"E10.trimOffspring")])],"isStart":true}),"instanceName":"1"});
            var Q3;
            Q3=makeQuery(id+"F2.opPattern","COPY",EDGE,{"derivedFrom":makeQuery(id+"F1.opExtrude","CAP_EDGE",EDGE,{"disambiguationData":[OSD([sQuery(id+"F0.wireOp",EDGE,"E19.trimOffspring")])],"isStart":true}),"instanceName":"1"});
            var Q4;
            Q4=makeQuery(id+"F2.opPattern","COPY",EDGE,{"derivedFrom":makeQuery(id+"F1.opExtrude","CAP_EDGE",EDGE,{"disambiguationData":[OSD([sQuery(id+"F0.wireOp",EDGE,"E42.trimOffspring")])],"isStart":true}),"instanceName":"1"});
            var Q5;
            Q5=makeQuery(id+"F2.opPattern","COPY",EDGE,{"derivedFrom":makeQuery(id+"F1.opExtrude","CAP_EDGE",EDGE,{"disambiguationData":[OSD([sQuery(id+"F0.wireOp",EDGE,"E41.trimOffspring")])],"isStart":true}),"instanceName":"1"});
            var Q6;
            Q6=makeQuery(id+"F2.opPattern","COPY",EDGE,{"derivedFrom":makeQuery(id+"F1.opExtrude","CAP_EDGE",EDGE,{"disambiguationData":[OSD([sQuery(id+"F0.wireOp",EDGE,"E40.trimOffspring")])],"isStart":true}),"instanceName":"1"});
            var Q7;
            Q7=makeQuery(id+"F2.opPattern","COPY",EDGE,{"derivedFrom":makeQuery(id+"F1.opExtrude","CAP_EDGE",EDGE,{"disambiguationData":[OSD([sQuery(id+"F0.wireOp",EDGE,"E27.trimOffspring")])],"isStart":true}),"instanceName":"1"});
            var Q8;
            Q8=makeQuery(id+"F2.opPattern","COPY",EDGE,{"derivedFrom":makeQuery(id+"F1.opExtrude","CAP_EDGE",EDGE,{"disambiguationData":[OSD([sQuery(id+"F0.wireOp",EDGE,"E26.trimOffspring")])],"isStart":true}),"instanceName":"1"});
            var Q9;
            Q9=makeQuery(id+"F2.opPattern","COPY",EDGE,{"derivedFrom":makeQuery(id+"F1.opExtrude","CAP_EDGE",EDGE,{"disambiguationData":[OSD([sQuery(id+"F0.wireOp",EDGE,"E0.top")])],"isStart":true}),"instanceName":"1"});
            var Q10;
            Q10=makeQuery(id+"F2.opPattern","COPY",EDGE,{"derivedFrom":makeQuery(id+"F1.opExtrude","CAP_EDGE",EDGE,{"disambiguationData":[OSD([sQuery(id+"F0.wireOp",EDGE,"E51.trimOffspring")])],"isStart":true}),"instanceName":"1"});
            var Q11;
            Q11=makeQuery(id+"F2.opPattern","COPY",EDGE,{"derivedFrom":makeQuery(id+"F1.opExtrude","CAP_EDGE",EDGE,{"disambiguationData":[OSD([sQuery(id+"F0.wireOp",EDGE,"E50.trimOffspring")])],"isStart":true}),"instanceName":"1"});
            var Q12;
            Q12=makeQuery(id+"F2.opPattern","COPY",EDGE,{"derivedFrom":makeQuery(id+"F1.opExtrude","CAP_EDGE",EDGE,{"disambiguationData":[OSD([sQuery(id+"F0.wireOp",EDGE,"E0.left")])],"isStart":true}),"instanceName":"1"});
            var Q13;
            Q13=makeQuery(id+"F2.opPattern","COPY",EDGE,{"derivedFrom":makeQuery(id+"F1.opExtrude","CAP_EDGE",EDGE,{"disambiguationData":[OSD([sQuery(id+"F0.wireOp",EDGE,"E13.trimOffspring")])],"isStart":true}),"instanceName":"1"});
            fillet(context, id + "F13", {"entities" : qUnion([Q0, Q1, Q2, Q3, Q4, Q5, Q6, Q7, Q8, Q9, Q10, Q11, Q12, Q13]), "radius" : 6.35 * mm, "tangentPropagation" : true, "allowEdgeOverflow" : false});
        }
        {
            var Q0;
            Q0=makeQuery(id+"F4.opExtrude","CAP_EDGE",EDGE,{"disambiguationData":[OSD([sQuery(id+"F3.wireOp",EDGE,"E52.left")])],"isStart":false});
            var Q1;
            Q1=makeQuery(id+"F4.opExtrude","CAP_EDGE",EDGE,{"disambiguationData":[OSD([sQuery(id+"F3.wireOp",EDGE,"E52.bottom")])],"isStart":false});
            var Q2;
            Q2=makeQuery(id+"F4.opExtrude","CAP_EDGE",EDGE,{"disambiguationData":[OSD([sQuery(id+"F3.wireOp",EDGE,"E95.trimOffspring")])],"isStart":false});
            var Q3;
            Q3=makeQuery(id+"F4.opExtrude","CAP_EDGE",EDGE,{"disambiguationData":[OSD([sQuery(id+"F3.wireOp",EDGE,"E97.trimOffspring")])],"isStart":false});
            var Q4;
            Q4=makeQuery(id+"F4.opExtrude","CAP_EDGE",EDGE,{"disambiguationData":[OSD([sQuery(id+"F3.wireOp",EDGE,"E52.top")])],"isStart":false});
            var Q5;
            Q5=makeQuery(id+"F4.opExtrude","CAP_EDGE",EDGE,{"disambiguationData":[OSD([sQuery(id+"F3.wireOp",EDGE,"E94.trimOffspring")])],"isStart":false});
            var Q6;
            Q6=makeQuery(id+"F4.opExtrude","CAP_EDGE",EDGE,{"disambiguationData":[OSD([sQuery(id+"F3.wireOp",EDGE,"E85.trimOffspring")])],"isStart":false});
            var Q7;
            Q7=makeQuery(id+"F4.opExtrude","CAP_EDGE",EDGE,{"disambiguationData":[OSD([sQuery(id+"F3.wireOp",EDGE,"E92.trimOffspring")])],"isStart":false});
            var Q8;
            Q8=makeQuery(id+"F4.opExtrude","CAP_EDGE",EDGE,{"disambiguationData":[OSD([sQuery(id+"F3.wireOp",EDGE,"E90.trimOffspring")])],"isStart":false});
            var Q9;
            Q9=makeQuery(id+"F4.opExtrude","CAP_EDGE",EDGE,{"disambiguationData":[OSD([sQuery(id+"F3.wireOp",EDGE,"E88.trimOffspring")])],"isStart":false});
            var Q10;
            Q10=makeQuery(id+"F4.opExtrude","CAP_EDGE",EDGE,{"disambiguationData":[OSD([sQuery(id+"F3.wireOp",EDGE,"E87.trimOffspring")])],"isStart":false});
            var Q11;
            Q11=makeQuery(id+"F4.opExtrude","CAP_EDGE",EDGE,{"disambiguationData":[OSD([sQuery(id+"F3.wireOp",EDGE,"E83.trimOffspring")])],"isStart":false});
            var Q12;
            Q12=makeQuery(id+"F4.opExtrude","CAP_EDGE",EDGE,{"disambiguationData":[OSD([sQuery(id+"F3.wireOp",EDGE,"E81.trimOffspring")])],"isStart":false});
            var Q13;
            Q13=makeQuery(id+"F4.opExtrude","CAP_EDGE",EDGE,{"disambiguationData":[OSD([sQuery(id+"F3.wireOp",EDGE,"E79.trimOffspring")])],"isStart":false});
            var Q14;
            Q14=makeQuery(id+"F4.opExtrude","CAP_EDGE",EDGE,{"disambiguationData":[OSD([sQuery(id+"F3.wireOp",EDGE,"E52.right")])],"isStart":false});
            var Q15;
            Q15=makeQuery(id+"F4.opExtrude","CAP_EDGE",EDGE,{"disambiguationData":[OSD([sQuery(id+"F3.wireOp",EDGE,"E78.trimOffspring")])],"isStart":false});
            fillet(context, id + "F14", {"entities" : qUnion([Q0, Q1, Q2, Q3, Q4, Q5, Q6, Q7, Q8, Q9, Q10, Q11, Q12, Q13, Q14, Q15]), "radius" : 5.08 * mm, "tangentPropagation" : true, "allowEdgeOverflow" : false});
        }
        {
            var Q0;
            Q0=makeQuery(id+"F4.opExtrude","SWEPT_EDGE",EDGE,{"disambiguationData":[OSD([sQuery(id+"F3.wireOp",EDGE,"E87.trimOffspring"),sQuery(id+"F3.wireOp",EDGE,"E88.trimOffspring")])]});
            var Q1;
            Q1=makeQuery(id+"F4.opExtrude","SWEPT_EDGE",EDGE,{"disambiguationData":[OSD([sQuery(id+"F3.wireOp",EDGE,"E52.right"),sQuery(id+"F3.wireOp",EDGE,"E78.trimOffspring")])]});
            var Q2;
            Q2=makeQuery(id+"F4.opExtrude","SWEPT_EDGE",EDGE,{"disambiguationData":[OSD([sQuery(id+"F3.wireOp",EDGE,"E52.bottom"),sQuery(id+"F3.wireOp",EDGE,"E52.left")])]});
            var Q3;
            Q3=makeQuery(id+"F4.opExtrude","SWEPT_EDGE",EDGE,{"disambiguationData":[OSD([sQuery(id+"F3.wireOp",EDGE,"E52.top"),sQuery(id+"F3.wireOp",EDGE,"E97.trimOffspring")])]});
            fillet(context, id + "F15", {"entities" : qUnion([Q0, Q1, Q2, Q3]), "radius" : 6.35 * mm, "tangentPropagation" : true, "allowEdgeOverflow" : false});
        }
        {
            var Q0;
            Q0=makeQuery(id+"F5.opPattern","COPY",EDGE,{"derivedFrom":makeQuery(id+"F4.opExtrude","SWEPT_EDGE",EDGE,{"disambiguationData":[OSD([sQuery(id+"F3.wireOp",EDGE,"E52.top"),sQuery(id+"F3.wireOp",EDGE,"E97.trimOffspring")])]}),"instanceName":"1"});
            var Q1;
            Q1=makeQuery(id+"F5.opPattern","COPY",EDGE,{"derivedFrom":makeQuery(id+"F4.opExtrude","SWEPT_EDGE",EDGE,{"disambiguationData":[OSD([sQuery(id+"F3.wireOp",EDGE,"E52.bottom"),sQuery(id+"F3.wireOp",EDGE,"E52.left")])]}),"instanceName":"1"});
            var Q2;
            Q2=makeQuery(id+"F5.opPattern","COPY",EDGE,{"derivedFrom":makeQuery(id+"F4.opExtrude","SWEPT_EDGE",EDGE,{"disambiguationData":[OSD([sQuery(id+"F3.wireOp",EDGE,"E52.right"),sQuery(id+"F3.wireOp",EDGE,"E78.trimOffspring")])]}),"instanceName":"1"});
            var Q3;
            Q3=makeQuery(id+"F5.opPattern","COPY",EDGE,{"derivedFrom":makeQuery(id+"F4.opExtrude","SWEPT_EDGE",EDGE,{"disambiguationData":[OSD([sQuery(id+"F3.wireOp",EDGE,"E87.trimOffspring"),sQuery(id+"F3.wireOp",EDGE,"E88.trimOffspring")])]}),"instanceName":"1"});
            fillet(context, id + "F16", {"entities" : qUnion([Q0, Q1, Q2, Q3]), "radius" : 6.35 * mm, "tangentPropagation" : true, "allowEdgeOverflow" : false});
        }
    });
